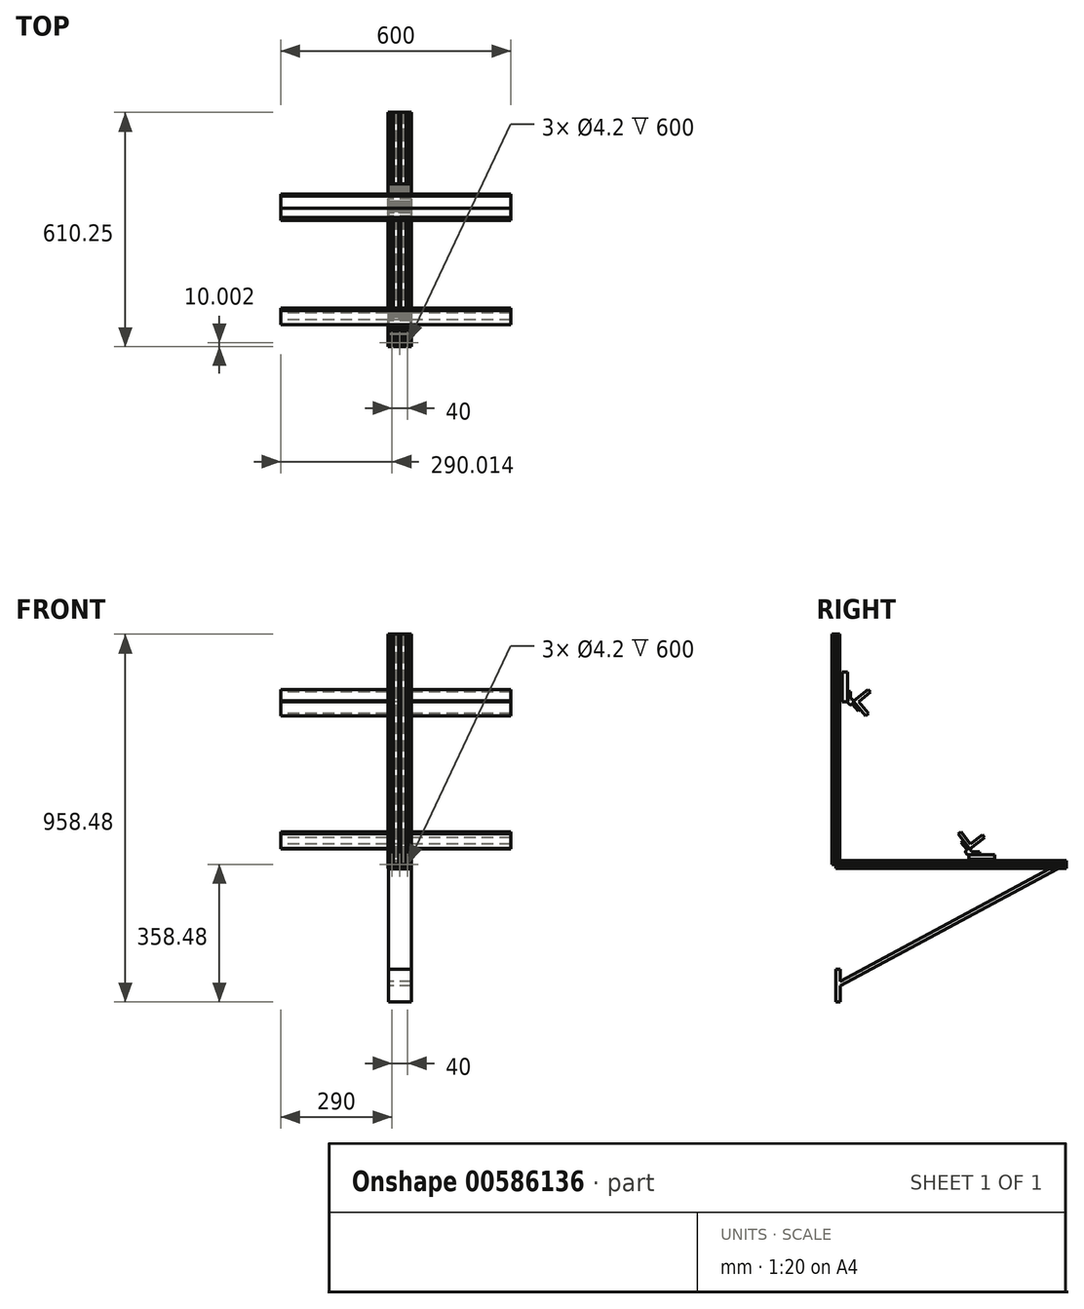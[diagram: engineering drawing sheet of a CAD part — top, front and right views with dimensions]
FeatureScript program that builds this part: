
annotation { "Feature Type Name" : "Feature", "Feature Type Description" : "" }
export const myFeature = defineFeature(function(context is Context, id is Id, definition is map)
    precondition{}
    {
        {
            var Q0;
            Q0=qCreatedBy(makeId("Front.planeOp"),FACE);
            var sketch = newSketch(context, id + "F0", { "sketchPlane" : qUnion([Q0])});
            skLineSegment(sketch, "E0.bottom", {"start": v(20, -10) * mm, "end": v(13, -10) * mm});
            skLineSegment(sketch, "E0.top", {"start": v(20, 10) * mm, "end": v(13, 10) * mm});
            skLineSegment(sketch, "E0.right", {"start": v(-20, -10) * mm, "end": v(-20, -3) * mm});
            skPoint(sketch, "E0.middle", {"position": v(0, 0) * mm});
            skLineSegment(sketch, "E1.bottom", {"start": v(-8, -3) * mm, "end": v(-12, -3) * mm});
            skLineSegment(sketch, "E1.top", {"start": v(-8, 3) * mm, "end": v(-12, 3) * mm});
            skLineSegment(sketch, "E1.left", {"start": v(-7, -2) * mm, "end": v(-7, 2) * mm});
            skLineSegment(sketch, "E1.right", {"start": v(-13, -2) * mm, "end": v(-13, 2) * mm});
            skPoint(sketch, "E1.middle", {"position": v(-10, 0) * mm});
            skLineSegment(sketch, "E2.bottom", {"start": v(8, -3) * mm, "end": v(12, -3) * mm});
            skLineSegment(sketch, "E2.top", {"start": v(8, 3) * mm, "end": v(12, 3) * mm});
            skLineSegment(sketch, "E2.left", {"start": v(7, -2) * mm, "end": v(7, 2) * mm});
            skLineSegment(sketch, "E2.right", {"start": v(13, -2) * mm, "end": v(13, 2) * mm});
            skPoint(sketch, "E2.middle", {"position": v(10, 0) * mm});
            skLineSegment(sketch, "E3.bottom", {"start": v(-3, -8) * mm, "end": v(-7, -8) * mm});
            skLineSegment(sketch, "E3.top", {"start": v(-3, 8) * mm, "end": v(-7, 8) * mm});
            skLineSegment(sketch, "E3.right", {"start": v(-18, -6) * mm, "end": v(-18, -3) * mm});
            skLineSegment(sketch, "E4.bottom", {"start": v(3, -8) * mm, "end": v(7, -8) * mm});
            skLineSegment(sketch, "E4.top", {"start": v(3, 8) * mm, "end": v(4, 8) * mm});
            skLineSegment(sketch, "E5.bottom", {"start": v(-20, 10) * mm, "end": v(-16, 10) * mm});
            skLineSegment(sketch, "E5.top", {"start": v(-18, 6) * mm, "end": v(-17, 6) * mm});
            skLineSegment(sketch, "E5.right", {"start": v(-16, 8) * mm, "end": v(-16, 7) * mm});
            skPoint(sketch, "E5.middle", {"position": v(-18, 8) * mm});
            skLineSegment(sketch, "E6.bottom", {"start": v(-20, 10) * mm, "end": v(-19, 10) * mm});
            skLineSegment(sketch, "E7.top", {"start": v(-1, -10) * mm, "end": v(0, -10) * mm});
            skLineSegment(sketch, "E8", {"start": v(-16, 7) * mm, "end": v(-12, 3) * mm});
            skLineSegment(sketch, "E9", {"start": v(-3, -8) * mm, "end": v(-8, -3) * mm});
            skLineSegment(sketch, "E10.MirrorCS", {"start": v(-16, -7) * mm, "end": v(-12, -3) * mm});
            skLineSegment(sketch, "E11.MirrorCS", {"start": v(-3, 8) * mm, "end": v(-8, 3) * mm});
            skLineSegment(sketch, "E12.MirrorCS", {"start": v(3, 8) * mm, "end": v(8, 3) * mm});
            skLineSegment(sketch, "E13.MirrorCS", {"start": v(3, -8) * mm, "end": v(8, -3) * mm});
            skLineSegment(sketch, "E14.bottom", {"start": v(20, 10) * mm, "end": v(16, 10) * mm});
            skPoint(sketch, "E14.middle", {"position": v(18, 8) * mm});
            skLineSegment(sketch, "E15.bottom", {"start": v(20, -10) * mm, "end": v(16, -10) * mm});
            skPoint(sketch, "E15.middle", {"position": v(18, -8) * mm});
            skPoint(sketch, "E16.orphan", {"position": v(13, 3) * mm});
            skLineSegment(sketch, "E17.trimOffspring", {"start": v(7, 2) * mm, "end": v(2, 7) * mm});
            skLineSegment(sketch, "E18.trimOffspring", {"start": v(7, -2) * mm, "end": v(2, -7) * mm});
            skPoint(sketch, "E19.orphan", {"position": v(13, -3) * mm});
            skPoint(sketch, "E20.orphan", {"position": v(7, 3) * mm});
            skPoint(sketch, "E21.orphan", {"position": v(7, -3) * mm});
            skPoint(sketch, "E22.orphan", {"position": v(19, -10) * mm});
            skPoint(sketch, "E7.left.start.orphan", {"position": v(-1, -9) * mm});
            skPoint(sketch, "E23.orphan", {"position": v(-2, -8) * mm});
            skPoint(sketch, "E24.orphan", {"position": v(-18, -8) * mm});
            skPoint(sketch, "E25.orphan", {"position": v(-19, -10) * mm});
            skPoint(sketch, "E26.orphan", {"position": v(-20, -9) * mm});
            skPoint(sketch, "E27.orphan", {"position": v(-16, 6) * mm});
            skPoint(sketch, "E28.orphan", {"position": v(-1, 10) * mm});
            skPoint(sketch, "E29.orphan", {"position": v(0, 9) * mm});
            skPoint(sketch, "E30.orphan", {"position": v(1, 10) * mm});
            skPoint(sketch, "E31.orphan", {"position": v(2, 8) * mm});
            skPoint(sketch, "E32.orphan", {"position": v(-2, 8) * mm});
            skPoint(sketch, "E33.orphan", {"position": v(0, -9) * mm});
            skPoint(sketch, "E34.orphan", {"position": v(1, -10) * mm});
            skPoint(sketch, "E35.orphan", {"position": v(2, -8) * mm});
            skLineSegment(sketch, "E36", {"start": v(-1, -8) * mm, "end": v(1, -8) * mm});
            skLineSegment(sketch, "E37", {"start": v(1, 8) * mm, "end": v(-1, 8) * mm});
            skLineSegment(sketch, "E38", {"start": v(-2, 7) * mm, "end": v(-1, 8) * mm});
            skLineSegment(sketch, "E39", {"start": v(2, 7) * mm, "end": v(1, 8) * mm});
            skLineSegment(sketch, "E40", {"start": v(-2, -7) * mm, "end": v(-1, -8) * mm});
            skLineSegment(sketch, "E41", {"start": v(2, -7) * mm, "end": v(1, -8) * mm});
            skPoint(sketch, "E42.orphan", {"position": v(-13, 3) * mm});
            skPoint(sketch, "E43.orphan", {"position": v(-7, 3) * mm});
            skPoint(sketch, "E44.orphan", {"position": v(-7, -3) * mm});
            skPoint(sketch, "E45.orphan", {"position": v(-13, -3) * mm});
            skLineSegment(sketch, "E46.trimOffspring", {"start": v(-13, 2) * mm, "end": v(-17, 6) * mm});
            skLineSegment(sketch, "E47.trimOffspring", {"start": v(-7, -2) * mm, "end": v(-2, -7) * mm});
            skLineSegment(sketch, "E48.trimOffspring", {"start": v(-7, 2) * mm, "end": v(-2, 7) * mm});
            skLineSegment(sketch, "E49.trimOffspring", {"start": v(-13, -2) * mm, "end": v(-17, -6) * mm});
            skLineSegment(sketch, "E50.bottom", {"start": v(-20, -10) * mm, "end": v(-16, -10) * mm});
            skLineSegment(sketch, "E50.top", {"start": v(-18, -6) * mm, "end": v(-17, -6) * mm});
            skLineSegment(sketch, "E50.left", {"start": v(-20, -10) * mm, "end": v(-20, -6) * mm});
            skLineSegment(sketch, "E50.right", {"start": v(-16, -8) * mm, "end": v(-16, -7) * mm});
            skPoint(sketch, "E51.orphan", {"position": v(-16, -6) * mm});
            skLineSegment(sketch, "E52", {"start": v(-13, -8) * mm, "end": v(-13, -10) * mm});
            skLineSegment(sketch, "E53", {"start": v(-7, -8) * mm, "end": v(-7, -10) * mm});
            skLineSegment(sketch, "E54", {"start": v(-18, 3) * mm, "end": v(-20, 3) * mm});
            skLineSegment(sketch, "E55", {"start": v(-18, -3) * mm, "end": v(-20, -3) * mm});
            skLineSegment(sketch, "E56", {"start": v(-13, 8) * mm, "end": v(-13, 10) * mm});
            skLineSegment(sketch, "E57", {"start": v(-7, 8) * mm, "end": v(-7, 10) * mm});
            skLineSegment(sketch, "E58.MirrorCS", {"start": v(13, -8) * mm, "end": v(13, -10) * mm});
            skLineSegment(sketch, "E59.MirrorCS", {"start": v(7, -8) * mm, "end": v(7, -10) * mm});
            skLineSegment(sketch, "E60.trimOffspring", {"start": v(-18, 3) * mm, "end": v(-18, 6) * mm});
            skLineSegment(sketch, "E61.trimOffspring", {"start": v(-20, 3) * mm, "end": v(-20, 7.62) * mm});
            skLineSegment(sketch, "E62.trimOffspring", {"start": v(-13, 10) * mm, "end": v(-20, 10) * mm});
            skLineSegment(sketch, "E63.trimOffspring", {"start": v(-13, 8) * mm, "end": v(-16, 8) * mm});
            skLineSegment(sketch, "E64.trimOffspring", {"start": v(-13, -8) * mm, "end": v(-16, -8) * mm});
            skLineSegment(sketch, "E65.trimOffspring", {"start": v(-13, -10) * mm, "end": v(-20, -10) * mm});
            skLineSegment(sketch, "E66.trimOffspring", {"start": v(13, -8) * mm, "end": v(16, -8) * mm});
            skLineSegment(sketch, "E67.trimOffspring", {"start": v(7, -10) * mm, "end": v(-7, -10) * mm});
            skCircle(sketch, "E68", {"center": v(-10, 0) * mm, "radius": 2.1 * mm});
            skCircle(sketch, "E69.MirrorC", {"center": v(10, 0) * mm, "radius": 2.1 * mm});
            skLineSegment(sketch, "E70.trimOffspring", {"start": v(-20, 7.62) * mm, "end": v(-20, 6) * mm});
            skLineSegment(sketch, "E71", {"start": v(-20, 10) * mm, "end": v(-20, 7.62) * mm});
            skLineSegment(sketch, "E72.MirrorCS", {"start": v(17, 8) * mm, "end": v(12, 3) * mm});
            skLineSegment(sketch, "E73.MirrorCS", {"start": v(13, 2) * mm, "end": v(18, 7) * mm});
            skLineSegment(sketch, "E74.MirrorCS", {"start": v(17, 8) * mm, "end": v(13, 8) * mm});
            skLineSegment(sketch, "E75.MirrorCS", {"start": v(17, -8) * mm, "end": v(12, -3) * mm});
            skLineSegment(sketch, "E76.MirrorCS", {"start": v(13, -2) * mm, "end": v(18, -7) * mm});
            skLineSegment(sketch, "E77.MirrorCS", {"start": v(17, -8) * mm, "end": v(13, -8) * mm});
            skLineSegment(sketch, "E78.MirrorCS", {"start": v(13, -10) * mm, "end": v(27, -10) * mm});
            skLineSegment(sketch, "E79.MirrorCS", {"start": v(40, 10) * mm, "end": v(39, 10) * mm});
            skLineSegment(sketch, "E80.MirrorCS", {"start": v(38, 6) * mm, "end": v(37, 6) * mm});
            skLineSegment(sketch, "E81.MirrorCS", {"start": v(36, 8) * mm, "end": v(36, 7) * mm});
            skLineSegment(sketch, "E82.MirrorCS", {"start": v(40, 10) * mm, "end": v(40, 7.62) * mm});
            skLineSegment(sketch, "E83.MirrorCS", {"start": v(21, -8) * mm, "end": v(19, -8) * mm});
            skLineSegment(sketch, "E84.MirrorCS", {"start": v(38, 3) * mm, "end": v(40, 3) * mm});
            skLineSegment(sketch, "E85.MirrorCS", {"start": v(36, -8) * mm, "end": v(36, -7) * mm});
            skLineSegment(sketch, "E86.MirrorCS", {"start": v(22, -7) * mm, "end": v(21, -8) * mm});
            skLineSegment(sketch, "E87.MirrorCS", {"start": v(22, 7) * mm, "end": v(21, 8) * mm});
            skLineSegment(sketch, "E88.MirrorCS", {"start": v(19, 8) * mm, "end": v(21, 8) * mm});
            skLineSegment(sketch, "E89.MirrorCS", {"start": v(38, -3) * mm, "end": v(40, -3) * mm});
            skLineSegment(sketch, "E90.MirrorCS", {"start": v(33, 8) * mm, "end": v(33, 10) * mm});
            skLineSegment(sketch, "E91.MirrorCS", {"start": v(38, -6) * mm, "end": v(37, -6) * mm});
            skLineSegment(sketch, "E92.MirrorCS", {"start": v(27, -8) * mm, "end": v(27, -10) * mm});
            skLineSegment(sketch, "E93.MirrorCS", {"start": v(27, 8) * mm, "end": v(27, 10) * mm});
            skLineSegment(sketch, "E94.MirrorCS", {"start": v(18, -7) * mm, "end": v(19, -8) * mm});
            skLineSegment(sketch, "E95.MirrorCS", {"start": v(18, 7) * mm, "end": v(19, 8) * mm});
            skLineSegment(sketch, "E96.MirrorCS", {"start": v(33, -8) * mm, "end": v(33, -10) * mm});
            skLineSegment(sketch, "E97.MirrorCS", {"start": v(21, -10) * mm, "end": v(20, -10) * mm});
            skLineSegment(sketch, "E98.MirrorCS", {"start": v(40, 7.62) * mm, "end": v(40, 6) * mm});
            skLineSegment(sketch, "E99.MirrorCS", {"start": v(40, -10) * mm, "end": v(40, -6) * mm});
            skPoint(sketch, "E100.MirrorP", {"position": v(38, -8) * mm});
            skPoint(sketch, "E101.MirrorP", {"position": v(20, 9) * mm});
            skPoint(sketch, "E102.MirrorP", {"position": v(30, 0) * mm});
            skPoint(sketch, "E103.MirrorP", {"position": v(20, -9) * mm});
            skLineSegment(sketch, "E104.MirrorCS", {"start": v(33, -8) * mm, "end": v(36, -8) * mm});
            skLineSegment(sketch, "E105.MirrorCS", {"start": v(27, -2) * mm, "end": v(27, 2) * mm});
            skLineSegment(sketch, "E106.MirrorCS", {"start": v(28, -3) * mm, "end": v(32, -3) * mm});
            skLineSegment(sketch, "E107.MirrorCS", {"start": v(28, 3) * mm, "end": v(32, 3) * mm});
            skLineSegment(sketch, "E108.MirrorCS", {"start": v(40, -10) * mm, "end": v(40, -3) * mm});
            skLineSegment(sketch, "E109.MirrorCS", {"start": v(38, -6) * mm, "end": v(38, -3) * mm});
            skLineSegment(sketch, "E110.MirrorCS", {"start": v(27, -2) * mm, "end": v(22, -7) * mm});
            skLineSegment(sketch, "E111.MirrorCS", {"start": v(40, 3) * mm, "end": v(40, 7.62) * mm});
            skLineSegment(sketch, "E112.MirrorCS", {"start": v(23, -8) * mm, "end": v(28, -3) * mm});
            skPoint(sketch, "E113.MirrorP", {"position": v(22, 8) * mm});
            skPoint(sketch, "E114.MirrorP", {"position": v(40, -9) * mm});
            skPoint(sketch, "E115.MirrorP", {"position": v(38, 8) * mm});
            skCircle(sketch, "E116.MirrorC", {"center": v(30, 0) * mm, "radius": 2.1 * mm});
            skPoint(sketch, "E117.MirrorP", {"position": v(27, -3) * mm});
            skPoint(sketch, "E118.MirrorP", {"position": v(27, 3) * mm});
            skPoint(sketch, "E119.MirrorP", {"position": v(22, -8) * mm});
            skPoint(sketch, "E120.MirrorP", {"position": v(36, -6) * mm});
            skLineSegment(sketch, "E121.MirrorCS", {"start": v(23, 8) * mm, "end": v(27, 8) * mm});
            skLineSegment(sketch, "E122.MirrorCS", {"start": v(23, -8) * mm, "end": v(27, -8) * mm});
            skLineSegment(sketch, "E123.MirrorCS", {"start": v(33, -2) * mm, "end": v(33, 2) * mm});
            skLineSegment(sketch, "E124.MirrorCS", {"start": v(23, 8) * mm, "end": v(28, 3) * mm});
            skLineSegment(sketch, "E125.MirrorCS", {"start": v(38, 3) * mm, "end": v(38, 6) * mm});
            skPoint(sketch, "E126.MirrorP", {"position": v(39, -10) * mm});
            skPoint(sketch, "E127.MirrorP", {"position": v(21, -9) * mm});
            skPoint(sketch, "E128.MirrorP", {"position": v(33, 3) * mm});
            skPoint(sketch, "E129.MirrorP", {"position": v(19, 10) * mm});
            skLineSegment(sketch, "E130.MirrorCS", {"start": v(33, -2) * mm, "end": v(37, -6) * mm});
            skLineSegment(sketch, "E131.MirrorCS", {"start": v(33, 8) * mm, "end": v(36, 8) * mm});
            skLineSegment(sketch, "E132.MirrorCS", {"start": v(40, -10) * mm, "end": v(36, -10) * mm});
            skLineSegment(sketch, "E133.MirrorCS", {"start": v(40, 10) * mm, "end": v(36, 10) * mm});
            skPoint(sketch, "E134.MirrorP", {"position": v(36, 6) * mm});
            skLineSegment(sketch, "E135.MirrorCS", {"start": v(27, 2) * mm, "end": v(22, 7) * mm});
            skLineSegment(sketch, "E136.MirrorCS", {"start": v(36, -7) * mm, "end": v(32, -3) * mm});
            skLineSegment(sketch, "E137.MirrorCS", {"start": v(33, 10) * mm, "end": v(40, 10) * mm});
            skLineSegment(sketch, "E138.MirrorCS", {"start": v(33, -10) * mm, "end": v(40, -10) * mm});
            skPoint(sketch, "E139.MirrorP", {"position": v(21, 10) * mm});
            skLineSegment(sketch, "E140.MirrorCS", {"start": v(33, 2) * mm, "end": v(37, 6) * mm});
            skLineSegment(sketch, "E141.MirrorCS", {"start": v(36, 7) * mm, "end": v(32, 3) * mm});
            skPoint(sketch, "E142.MirrorP", {"position": v(20, 0) * mm});
            skPoint(sketch, "E143.MirrorP", {"position": v(33, -3) * mm});
            skLineSegment(sketch, "E144.MirrorCS", {"start": v(0, 10) * mm, "end": v(1, 10) * mm});
            skLineSegment(sketch, "E145.MirrorCS", {"start": v(13, 8) * mm, "end": v(13, 10) * mm});
            skLineSegment(sketch, "E146.MirrorCS", {"start": v(7, 8) * mm, "end": v(7, 10) * mm});
            skLineSegment(sketch, "E147.trimOffspring", {"start": v(7, 10) * mm, "end": v(-7, 10) * mm});
            skLineSegment(sketch, "E148.trimOffspring", {"start": v(13, 10) * mm, "end": v(27, 10) * mm});
            skLineSegment(sketch, "E149.trimOffspring", {"start": v(13, 8) * mm, "end": v(16, 8) * mm});
            skLineSegment(sketch, "E150.trimOffspring", {"start": v(7, 8) * mm, "end": v(4, 8) * mm});
            skPoint(sketch, "E151.start.orphan", {"position": v(10, 3) * mm});
            skPoint(sketch, "E152.start.orphan", {"position": v(13, 0) * mm});
            skSolve(sketch);
        }
        {
            var Q0;
            Q0=qSketchRegion(id+"F0",true);
            extrude(context, id + "F1", {"entities" : qUnion([Q0]), "oppositeDirection" : true, "depth" : 600 * mm, "offsetDistance" : 25.4 * mm});
        }
        {
            var Q0;
            Q0=qCreatedBy(makeId("Top.planeOp"),FACE);
            var sketch = newSketch(context, id + "F2", { "sketchPlane" : qUnion([Q0])});
            skLineSegment(sketch, "E153.bottom", {"start": v(20.01, -10.25) * mm, "end": v(13.01, -10.25) * mm});
            skLineSegment(sketch, "E153.top", {"start": v(20.01, 9.75) * mm, "end": v(13.01, 9.75) * mm});
            skLineSegment(sketch, "E153.right", {"start": v(-19.99, -10.25) * mm, "end": v(-19.99, -3.25) * mm});
            skPoint(sketch, "E153.middle", {"position": v(0.01, -0.25) * mm});
            skLineSegment(sketch, "E154.bottom", {"start": v(-7.99, -3.25) * mm, "end": v(-11.99, -3.25) * mm});
            skLineSegment(sketch, "E154.top", {"start": v(-7.99, 2.75) * mm, "end": v(-11.99, 2.75) * mm});
            skLineSegment(sketch, "E154.left", {"start": v(-6.99, -2.25) * mm, "end": v(-6.99, 1.75) * mm});
            skLineSegment(sketch, "E154.right", {"start": v(-12.99, -2.25) * mm, "end": v(-12.99, 1.75) * mm});
            skPoint(sketch, "E154.middle", {"position": v(-9.99, -0.25) * mm});
            skLineSegment(sketch, "E155.bottom", {"start": v(8.01, -3.25) * mm, "end": v(12.01, -3.25) * mm});
            skLineSegment(sketch, "E155.top", {"start": v(8.01, 2.75) * mm, "end": v(12.01, 2.75) * mm});
            skLineSegment(sketch, "E155.left", {"start": v(7.01, -2.25) * mm, "end": v(7.01, 1.75) * mm});
            skLineSegment(sketch, "E155.right", {"start": v(13.01, -2.25) * mm, "end": v(13.01, 1.75) * mm});
            skPoint(sketch, "E155.middle", {"position": v(10.01, -0.25) * mm});
            skLineSegment(sketch, "E156.bottom", {"start": v(-2.99, -8.25) * mm, "end": v(-6.99, -8.25) * mm});
            skLineSegment(sketch, "E156.top", {"start": v(-2.99, 7.75) * mm, "end": v(-6.99, 7.75) * mm});
            skLineSegment(sketch, "E156.right", {"start": v(-17.99, -6.25) * mm, "end": v(-17.99, -3.25) * mm});
            skLineSegment(sketch, "E157.bottom", {"start": v(3.01, -8.25) * mm, "end": v(7.01, -8.25) * mm});
            skLineSegment(sketch, "E157.top", {"start": v(3.01, 7.75) * mm, "end": v(4.01, 7.75) * mm});
            skLineSegment(sketch, "E158.bottom", {"start": v(-19.99, 9.75) * mm, "end": v(-15.99, 9.75) * mm});
            skLineSegment(sketch, "E158.top", {"start": v(-17.99, 5.75) * mm, "end": v(-16.99, 5.75) * mm});
            skLineSegment(sketch, "E158.right", {"start": v(-15.99, 7.75) * mm, "end": v(-15.99, 6.75) * mm});
            skPoint(sketch, "E158.middle", {"position": v(-17.99, 7.75) * mm});
            skLineSegment(sketch, "E159.bottom", {"start": v(-19.99, 9.75) * mm, "end": v(-18.99, 9.75) * mm});
            skLineSegment(sketch, "E160.top", {"start": v(-0.99, -10.25) * mm, "end": v(0.01, -10.25) * mm});
            skLineSegment(sketch, "E161", {"start": v(-15.99, 6.75) * mm, "end": v(-11.99, 2.75) * mm});
            skLineSegment(sketch, "E162", {"start": v(-2.99, -8.25) * mm, "end": v(-7.99, -3.25) * mm});
            skLineSegment(sketch, "E163.MirrorCS", {"start": v(-15.99, -7.25) * mm, "end": v(-11.99, -3.25) * mm});
            skLineSegment(sketch, "E164.MirrorCS", {"start": v(-2.99, 7.75) * mm, "end": v(-7.99, 2.75) * mm});
            skLineSegment(sketch, "E165.MirrorCS", {"start": v(3.01, 7.75) * mm, "end": v(8.01, 2.75) * mm});
            skLineSegment(sketch, "E166.MirrorCS", {"start": v(3.01, -8.25) * mm, "end": v(8.01, -3.25) * mm});
            skLineSegment(sketch, "E167.bottom", {"start": v(20.01, 9.75) * mm, "end": v(16.01, 9.75) * mm});
            skPoint(sketch, "E167.middle", {"position": v(18.01, 7.75) * mm});
            skLineSegment(sketch, "E168.bottom", {"start": v(20.01, -10.25) * mm, "end": v(16.01, -10.25) * mm});
            skPoint(sketch, "E168.middle", {"position": v(18.01, -8.25) * mm});
            skPoint(sketch, "E169.orphan", {"position": v(13.01, 2.75) * mm});
            skLineSegment(sketch, "E170.trimOffspring", {"start": v(7.01, 1.75) * mm, "end": v(2.01, 6.75) * mm});
            skLineSegment(sketch, "E171.trimOffspring", {"start": v(7.01, -2.25) * mm, "end": v(2.01, -7.25) * mm});
            skPoint(sketch, "E172.orphan", {"position": v(13.01, -3.25) * mm});
            skPoint(sketch, "E173.orphan", {"position": v(7.01, 2.75) * mm});
            skPoint(sketch, "E174.orphan", {"position": v(7.01, -3.25) * mm});
            skPoint(sketch, "E175.orphan", {"position": v(19.01, -10.25) * mm});
            skPoint(sketch, "E160.left.start.orphan", {"position": v(-0.99, -9.25) * mm});
            skPoint(sketch, "E176.orphan", {"position": v(-1.99, -8.25) * mm});
            skPoint(sketch, "E177.orphan", {"position": v(-17.99, -8.25) * mm});
            skPoint(sketch, "E178.orphan", {"position": v(-18.99, -10.25) * mm});
            skPoint(sketch, "E179.orphan", {"position": v(-19.99, -9.25) * mm});
            skPoint(sketch, "E180.orphan", {"position": v(-15.99, 5.75) * mm});
            skPoint(sketch, "E181.orphan", {"position": v(-0.99, 9.75) * mm});
            skPoint(sketch, "E182.orphan", {"position": v(0.01, 8.75) * mm});
            skPoint(sketch, "E183.orphan", {"position": v(1.01, 9.75) * mm});
            skPoint(sketch, "E184.orphan", {"position": v(2.01, 7.75) * mm});
            skPoint(sketch, "E185.orphan", {"position": v(-1.99, 7.75) * mm});
            skPoint(sketch, "E186.orphan", {"position": v(0.01, -9.25) * mm});
            skPoint(sketch, "E187.orphan", {"position": v(1.01, -10.25) * mm});
            skPoint(sketch, "E188.orphan", {"position": v(2.01, -8.25) * mm});
            skLineSegment(sketch, "E189", {"start": v(-0.99, -8.25) * mm, "end": v(1.01, -8.25) * mm});
            skLineSegment(sketch, "E190", {"start": v(1.01, 7.75) * mm, "end": v(-0.99, 7.75) * mm});
            skLineSegment(sketch, "E191", {"start": v(-1.99, 6.75) * mm, "end": v(-0.99, 7.75) * mm});
            skLineSegment(sketch, "E192", {"start": v(2.01, 6.75) * mm, "end": v(1.01, 7.75) * mm});
            skLineSegment(sketch, "E193", {"start": v(-1.99, -7.25) * mm, "end": v(-0.99, -8.25) * mm});
            skLineSegment(sketch, "E194", {"start": v(2.01, -7.25) * mm, "end": v(1.01, -8.25) * mm});
            skPoint(sketch, "E195.orphan", {"position": v(-12.99, 2.75) * mm});
            skPoint(sketch, "E196.orphan", {"position": v(-6.99, 2.75) * mm});
            skPoint(sketch, "E197.orphan", {"position": v(-6.99, -3.25) * mm});
            skPoint(sketch, "E198.orphan", {"position": v(-12.99, -3.25) * mm});
            skLineSegment(sketch, "E199.trimOffspring", {"start": v(-12.99, 1.75) * mm, "end": v(-16.99, 5.75) * mm});
            skLineSegment(sketch, "E200.trimOffspring", {"start": v(-6.99, -2.25) * mm, "end": v(-1.99, -7.25) * mm});
            skLineSegment(sketch, "E201.trimOffspring", {"start": v(-6.99, 1.75) * mm, "end": v(-1.99, 6.75) * mm});
            skLineSegment(sketch, "E202.trimOffspring", {"start": v(-12.99, -2.25) * mm, "end": v(-16.99, -6.25) * mm});
            skLineSegment(sketch, "E203.bottom", {"start": v(-19.99, -10.25) * mm, "end": v(-15.99, -10.25) * mm});
            skLineSegment(sketch, "E203.top", {"start": v(-17.99, -6.25) * mm, "end": v(-16.99, -6.25) * mm});
            skLineSegment(sketch, "E203.left", {"start": v(-19.99, -10.25) * mm, "end": v(-19.99, -6.25) * mm});
            skLineSegment(sketch, "E203.right", {"start": v(-15.99, -8.25) * mm, "end": v(-15.99, -7.25) * mm});
            skPoint(sketch, "E204.orphan", {"position": v(-15.99, -6.25) * mm});
            skLineSegment(sketch, "E205", {"start": v(-12.99, -8.25) * mm, "end": v(-12.99, -10.25) * mm});
            skLineSegment(sketch, "E206", {"start": v(-6.99, -8.25) * mm, "end": v(-6.99, -10.25) * mm});
            skLineSegment(sketch, "E207", {"start": v(-17.99, 2.75) * mm, "end": v(-19.99, 2.75) * mm});
            skLineSegment(sketch, "E208", {"start": v(-17.99, -3.25) * mm, "end": v(-19.99, -3.25) * mm});
            skLineSegment(sketch, "E209", {"start": v(-12.99, 7.75) * mm, "end": v(-12.99, 9.75) * mm});
            skLineSegment(sketch, "E210", {"start": v(-6.99, 7.75) * mm, "end": v(-6.99, 9.75) * mm});
            skLineSegment(sketch, "E211.MirrorCS", {"start": v(13.01, -8.25) * mm, "end": v(13.01, -10.25) * mm});
            skLineSegment(sketch, "E212.MirrorCS", {"start": v(7.01, -8.25) * mm, "end": v(7.01, -10.25) * mm});
            skLineSegment(sketch, "E213.trimOffspring", {"start": v(-17.99, 2.75) * mm, "end": v(-17.99, 5.75) * mm});
            skLineSegment(sketch, "E214.trimOffspring", {"start": v(-19.99, 2.75) * mm, "end": v(-19.99, 7.37) * mm});
            skLineSegment(sketch, "E215.trimOffspring", {"start": v(-12.99, 9.75) * mm, "end": v(-19.99, 9.75) * mm});
            skLineSegment(sketch, "E216.trimOffspring", {"start": v(-12.99, 7.75) * mm, "end": v(-15.99, 7.75) * mm});
            skLineSegment(sketch, "E217.trimOffspring", {"start": v(-12.99, -8.25) * mm, "end": v(-15.99, -8.25) * mm});
            skLineSegment(sketch, "E218.trimOffspring", {"start": v(-12.99, -10.25) * mm, "end": v(-19.99, -10.25) * mm});
            skLineSegment(sketch, "E219.trimOffspring", {"start": v(13.01, -8.25) * mm, "end": v(16.01, -8.25) * mm});
            skLineSegment(sketch, "E220.trimOffspring", {"start": v(7.01, -10.25) * mm, "end": v(-6.99, -10.25) * mm});
            skCircle(sketch, "E221", {"center": v(-9.99, -0.25) * mm, "radius": 2.1 * mm});
            skCircle(sketch, "E222.MirrorC", {"center": v(10.01, -0.25) * mm, "radius": 2.1 * mm});
            skLineSegment(sketch, "E223.trimOffspring", {"start": v(-19.99, 7.37) * mm, "end": v(-19.99, 5.75) * mm});
            skLineSegment(sketch, "E224", {"start": v(-19.99, 9.75) * mm, "end": v(-19.99, 7.37) * mm});
            skLineSegment(sketch, "E225.MirrorCS", {"start": v(17.01, 7.75) * mm, "end": v(12.01, 2.75) * mm});
            skLineSegment(sketch, "E226.MirrorCS", {"start": v(13.01, 1.75) * mm, "end": v(18.01, 6.75) * mm});
            skLineSegment(sketch, "E227.MirrorCS", {"start": v(17.01, 7.75) * mm, "end": v(13.01, 7.75) * mm});
            skLineSegment(sketch, "E228.MirrorCS", {"start": v(17.01, -8.25) * mm, "end": v(12.01, -3.25) * mm});
            skLineSegment(sketch, "E229.MirrorCS", {"start": v(13.01, -2.25) * mm, "end": v(18.01, -7.25) * mm});
            skLineSegment(sketch, "E230.MirrorCS", {"start": v(17.01, -8.25) * mm, "end": v(13.01, -8.25) * mm});
            skLineSegment(sketch, "E231.MirrorCS", {"start": v(13.01, -10.25) * mm, "end": v(27.01, -10.25) * mm});
            skLineSegment(sketch, "E232.MirrorCS", {"start": v(40.01, 9.75) * mm, "end": v(39.01, 9.75) * mm});
            skLineSegment(sketch, "E233.MirrorCS", {"start": v(38.01, 5.75) * mm, "end": v(37.01, 5.75) * mm});
            skLineSegment(sketch, "E234.MirrorCS", {"start": v(36.01, 7.75) * mm, "end": v(36.01, 6.75) * mm});
            skLineSegment(sketch, "E235.MirrorCS", {"start": v(40.01, 9.75) * mm, "end": v(40.01, 7.37) * mm});
            skLineSegment(sketch, "E236.MirrorCS", {"start": v(21.01, -8.25) * mm, "end": v(19.01, -8.25) * mm});
            skLineSegment(sketch, "E237.MirrorCS", {"start": v(38.01, 2.75) * mm, "end": v(40.01, 2.75) * mm});
            skLineSegment(sketch, "E238.MirrorCS", {"start": v(36.01, -8.25) * mm, "end": v(36.01, -7.25) * mm});
            skLineSegment(sketch, "E239.MirrorCS", {"start": v(22.01, -7.25) * mm, "end": v(21.01, -8.25) * mm});
            skLineSegment(sketch, "E240.MirrorCS", {"start": v(22.01, 6.75) * mm, "end": v(21.01, 7.75) * mm});
            skLineSegment(sketch, "E241.MirrorCS", {"start": v(19.01, 7.75) * mm, "end": v(21.01, 7.75) * mm});
            skLineSegment(sketch, "E242.MirrorCS", {"start": v(38.01, -3.25) * mm, "end": v(40.01, -3.25) * mm});
            skLineSegment(sketch, "E243.MirrorCS", {"start": v(33.01, 7.75) * mm, "end": v(33.01, 9.75) * mm});
            skLineSegment(sketch, "E244.MirrorCS", {"start": v(38.01, -6.25) * mm, "end": v(37.01, -6.25) * mm});
            skLineSegment(sketch, "E245.MirrorCS", {"start": v(27.01, -8.25) * mm, "end": v(27.01, -10.25) * mm});
            skLineSegment(sketch, "E246.MirrorCS", {"start": v(27.01, 7.75) * mm, "end": v(27.01, 9.75) * mm});
            skLineSegment(sketch, "E247.MirrorCS", {"start": v(18.01, -7.25) * mm, "end": v(19.01, -8.25) * mm});
            skLineSegment(sketch, "E248.MirrorCS", {"start": v(18.01, 6.75) * mm, "end": v(19.01, 7.75) * mm});
            skLineSegment(sketch, "E249.MirrorCS", {"start": v(33.01, -8.25) * mm, "end": v(33.01, -10.25) * mm});
            skLineSegment(sketch, "E250.MirrorCS", {"start": v(21.01, -10.25) * mm, "end": v(20.01, -10.25) * mm});
            skLineSegment(sketch, "E251.MirrorCS", {"start": v(40.01, 7.37) * mm, "end": v(40.01, 5.75) * mm});
            skLineSegment(sketch, "E252.MirrorCS", {"start": v(40.01, -10.25) * mm, "end": v(40.01, -6.25) * mm});
            skPoint(sketch, "E253.MirrorP", {"position": v(38.01, -8.25) * mm});
            skPoint(sketch, "E254.MirrorP", {"position": v(20.01, 8.75) * mm});
            skPoint(sketch, "E255.MirrorP", {"position": v(30.01, -0.25) * mm});
            skPoint(sketch, "E256.MirrorP", {"position": v(20.01, -9.25) * mm});
            skLineSegment(sketch, "E257.MirrorCS", {"start": v(33.01, -8.25) * mm, "end": v(36.01, -8.25) * mm});
            skLineSegment(sketch, "E258.MirrorCS", {"start": v(27.01, -2.25) * mm, "end": v(27.01, 1.75) * mm});
            skLineSegment(sketch, "E259.MirrorCS", {"start": v(28.01, -3.25) * mm, "end": v(32.01, -3.25) * mm});
            skLineSegment(sketch, "E260.MirrorCS", {"start": v(28.01, 2.75) * mm, "end": v(32.01, 2.75) * mm});
            skLineSegment(sketch, "E261.MirrorCS", {"start": v(40.01, -10.25) * mm, "end": v(40.01, -3.25) * mm});
            skLineSegment(sketch, "E262.MirrorCS", {"start": v(38.01, -6.25) * mm, "end": v(38.01, -3.25) * mm});
            skLineSegment(sketch, "E263.MirrorCS", {"start": v(27.01, -2.25) * mm, "end": v(22.01, -7.25) * mm});
            skLineSegment(sketch, "E264.MirrorCS", {"start": v(40.01, 2.75) * mm, "end": v(40.01, 7.37) * mm});
            skLineSegment(sketch, "E265.MirrorCS", {"start": v(23.01, -8.25) * mm, "end": v(28.01, -3.25) * mm});
            skPoint(sketch, "E266.MirrorP", {"position": v(22.01, 7.75) * mm});
            skPoint(sketch, "E267.MirrorP", {"position": v(40.01, -9.25) * mm});
            skPoint(sketch, "E268.MirrorP", {"position": v(38.01, 7.75) * mm});
            skCircle(sketch, "E269.MirrorC", {"center": v(30.01, -0.25) * mm, "radius": 2.1 * mm});
            skPoint(sketch, "E270.MirrorP", {"position": v(27.01, -3.25) * mm});
            skPoint(sketch, "E271.MirrorP", {"position": v(27.01, 2.75) * mm});
            skPoint(sketch, "E272.MirrorP", {"position": v(22.01, -8.25) * mm});
            skPoint(sketch, "E273.MirrorP", {"position": v(36.01, -6.25) * mm});
            skLineSegment(sketch, "E274.MirrorCS", {"start": v(23.01, 7.75) * mm, "end": v(27.01, 7.75) * mm});
            skLineSegment(sketch, "E275.MirrorCS", {"start": v(23.01, -8.25) * mm, "end": v(27.01, -8.25) * mm});
            skLineSegment(sketch, "E276.MirrorCS", {"start": v(33.01, -2.25) * mm, "end": v(33.01, 1.75) * mm});
            skLineSegment(sketch, "E277.MirrorCS", {"start": v(23.01, 7.75) * mm, "end": v(28.01, 2.75) * mm});
            skLineSegment(sketch, "E278.MirrorCS", {"start": v(38.01, 2.75) * mm, "end": v(38.01, 5.75) * mm});
            skPoint(sketch, "E279.MirrorP", {"position": v(39.01, -10.25) * mm});
            skPoint(sketch, "E280.MirrorP", {"position": v(21.01, -9.25) * mm});
            skPoint(sketch, "E281.MirrorP", {"position": v(33.01, 2.75) * mm});
            skPoint(sketch, "E282.MirrorP", {"position": v(19.01, 9.75) * mm});
            skLineSegment(sketch, "E283.MirrorCS", {"start": v(33.01, -2.25) * mm, "end": v(37.01, -6.25) * mm});
            skLineSegment(sketch, "E284.MirrorCS", {"start": v(33.01, 7.75) * mm, "end": v(36.01, 7.75) * mm});
            skLineSegment(sketch, "E285.MirrorCS", {"start": v(40.01, -10.25) * mm, "end": v(36.01, -10.25) * mm});
            skLineSegment(sketch, "E286.MirrorCS", {"start": v(40.01, 9.75) * mm, "end": v(36.01, 9.75) * mm});
            skPoint(sketch, "E287.MirrorP", {"position": v(36.01, 5.75) * mm});
            skLineSegment(sketch, "E288.MirrorCS", {"start": v(27.01, 1.75) * mm, "end": v(22.01, 6.75) * mm});
            skLineSegment(sketch, "E289.MirrorCS", {"start": v(36.01, -7.25) * mm, "end": v(32.01, -3.25) * mm});
            skLineSegment(sketch, "E290.MirrorCS", {"start": v(33.01, 9.75) * mm, "end": v(40.01, 9.75) * mm});
            skLineSegment(sketch, "E291.MirrorCS", {"start": v(33.01, -10.25) * mm, "end": v(40.01, -10.25) * mm});
            skPoint(sketch, "E292.MirrorP", {"position": v(21.01, 9.75) * mm});
            skLineSegment(sketch, "E293.MirrorCS", {"start": v(33.01, 1.75) * mm, "end": v(37.01, 5.75) * mm});
            skLineSegment(sketch, "E294.MirrorCS", {"start": v(36.01, 6.75) * mm, "end": v(32.01, 2.75) * mm});
            skPoint(sketch, "E295.MirrorP", {"position": v(20.01, -0.25) * mm});
            skPoint(sketch, "E296.MirrorP", {"position": v(33.01, -3.25) * mm});
            skLineSegment(sketch, "E297.MirrorCS", {"start": v(0.01, 9.75) * mm, "end": v(1.01, 9.75) * mm});
            skLineSegment(sketch, "E298.MirrorCS", {"start": v(13.01, 7.75) * mm, "end": v(13.01, 9.75) * mm});
            skLineSegment(sketch, "E299.MirrorCS", {"start": v(7.01, 7.75) * mm, "end": v(7.01, 9.75) * mm});
            skLineSegment(sketch, "E300.trimOffspring", {"start": v(7.01, 9.75) * mm, "end": v(-6.99, 9.75) * mm});
            skLineSegment(sketch, "E301.trimOffspring", {"start": v(13.01, 9.75) * mm, "end": v(27.01, 9.75) * mm});
            skLineSegment(sketch, "E302.trimOffspring", {"start": v(13.01, 7.75) * mm, "end": v(16.01, 7.75) * mm});
            skLineSegment(sketch, "E303.trimOffspring", {"start": v(7.01, 7.75) * mm, "end": v(4.01, 7.75) * mm});
            skPoint(sketch, "E304.start.orphan", {"position": v(10.01, 2.75) * mm});
            skPoint(sketch, "E305.start.orphan", {"position": v(13.01, -0.25) * mm});
            skSolve(sketch);
        }
        {
            var Q0;
            Q0=qSketchRegion(id+"F2",true);
            extrude(context, id + "F3", {"entities" : qUnion([Q0]), "operationType" : NewBodyOperationType.ADD, "depth" : 600 * mm, "offsetDistance" : 25.4 * mm});
        }
        {
            var Q0;
            Q0=qCreatedBy(makeId("Right.planeOp"),FACE);
            var sketch = newSketch(context, id + "F4", { "sketchPlane" : qUnion([Q0])});
            skLineSegment(sketch, "E306.right", {"start": v(577.1, -11.57) * mm, "end": v(577.1, -11.74) * mm});
            skLineSegment(sketch, "E307", {"start": v(555.61, -11.57) * mm, "end": v(11.28, -304.62) * mm});
            skLineSegment(sketch, "E308", {"start": v(577.42, -11.57) * mm, "end": v(11.28, -316.37) * mm});
            skLineSegment(sketch, "E309", {"start": v(0, -322.44) * mm, "end": v(0, -310.7) * mm});
            skLineSegment(sketch, "E310", {"start": v(555.61, -11.57) * mm, "end": v(577.42, -11.57) * mm});
            skPoint(sketch, "E311.orphan", {"position": v(577.1, 0) * mm});
            skPoint(sketch, "E312.orphan", {"position": v(598.9, 0) * mm});
            skLineSegment(sketch, "E313.top", {"start": v(0, -358.48) * mm, "end": v(11.28, -358.48) * mm});
            skLineSegment(sketch, "E313.left", {"start": v(0, -291.08) * mm, "end": v(0, -358.48) * mm});
            skLineSegment(sketch, "E313.right", {"start": v(11.28, -291.08) * mm, "end": v(11.28, -304.62) * mm});
            skLineSegment(sketch, "E314.top", {"start": v(11.28, -272.73) * mm, "end": v(0, -272.73) * mm});
            skLineSegment(sketch, "E314.left", {"start": v(11.28, -291.08) * mm, "end": v(11.28, -272.73) * mm});
            skLineSegment(sketch, "E314.right", {"start": v(0, -291.08) * mm, "end": v(0, -272.73) * mm});
            skLineSegment(sketch, "E315.trimOffspring", {"start": v(11.28, -316.37) * mm, "end": v(11.28, -358.48) * mm});
            skSolve(sketch);
        }
        {
            var Q0;
            Q0=qSketchRegion(id+"F4",true);
            extrude(context, id + "F5", {"entities" : qUnion([Q0]), "depth" : 40.4 * mm, "offsetDistance" : 25.4 * mm, "hasSecondDirection" : true, "secondDirectionOppositeDirection" : true, "secondDirectionDepth" : 19.8 * mm});
        }
        {
            var Q0;
            Q0=qCreatedBy(makeId("Right.planeOp"),FACE);
            var sketch = newSketch(context, id + "F6", { "sketchPlane" : qUnion([Q0])});
            skLineSegment(sketch, "E316", {"start": v(31.2, 420.16) * mm, "end": v(339.93, 26.86) * mm});
            skLineSegment(sketch, "E317.bottom", {"start": v(345.64, 13.63) * mm, "end": v(413.27, 13.63) * mm});
            skLineSegment(sketch, "E317.top", {"start": v(345.64, 25.03) * mm, "end": v(413.27, 25.03) * mm});
            skLineSegment(sketch, "E317.left", {"start": v(345.64, 13.63) * mm, "end": v(345.64, 25.03) * mm});
            skLineSegment(sketch, "E317.right", {"start": v(413.27, 13.63) * mm, "end": v(413.27, 25.03) * mm});
            skCircle(sketch, "E318", {"center": v(345.64, 32.7) * mm, "radius": 7.67 * mm});
            skLineSegment(sketch, "E319", {"start": v(345.64, 32.7) * mm, "end": v(326.32, 57.32) * mm});
            skLineSegment(sketch, "E320", {"start": v(326.32, 57.32) * mm, "end": v(330.53, 60.62) * mm});
            skLineSegment(sketch, "E321", {"start": v(330.53, 60.62) * mm, "end": v(346.46, 40.32) * mm});
            skLineSegment(sketch, "E322", {"start": v(185.56, 223.5) * mm, "end": v(222.86, 252.78) * mm});
            skLineSegment(sketch, "E323.MirrorCS", {"start": v(38.23, 424.32) * mm, "end": v(57.55, 399.7) * mm});
            skLineSegment(sketch, "E324.MirrorCS", {"start": v(57.55, 399.7) * mm, "end": v(61.76, 403.01) * mm});
            skLineSegment(sketch, "E325.MirrorCS", {"start": v(61.76, 403.01) * mm, "end": v(45.83, 423.3) * mm});
            skCircle(sketch, "E326.MirrorC", {"center": v(38.23, 424.32) * mm, "radius": 7.67 * mm});
            skLineSegment(sketch, "E327.bottom", {"start": v(30.56, 424.32) * mm, "end": v(15.48, 424.32) * mm});
            skLineSegment(sketch, "E327.top", {"start": v(30.56, 502) * mm, "end": v(15.48, 502) * mm});
            skLineSegment(sketch, "E327.left", {"start": v(30.56, 424.32) * mm, "end": v(30.56, 502) * mm});
            skLineSegment(sketch, "E327.right", {"start": v(15.48, 424.32) * mm, "end": v(15.48, 502) * mm});
            skLineSegment(sketch, "E328.bottom", {"start": v(38.23, 424.32) * mm, "end": v(38.23, 424.32) * mm});
            skLineSegment(sketch, "E328.top", {"start": v(38.23, 451.2) * mm, "end": v(38.23, 451.2) * mm});
            skLineSegment(sketch, "E328.left", {"start": v(38.23, 424.32) * mm, "end": v(38.23, 451.2) * mm});
            skLineSegment(sketch, "E328.right", {"start": v(38.23, 424.32) * mm, "end": v(38.23, 451.2) * mm});
            skLineSegment(sketch, "E329.right", {"start": v(30.56, 451.2) * mm, "end": v(30.56, 451.2) * mm});
            skLineSegment(sketch, "E330", {"start": v(345.64, 32.7) * mm, "end": v(374.18, 32.7) * mm});
            skLineSegment(sketch, "E331.bottom", {"start": v(38.23, 451.2) * mm, "end": v(30.95, 451.2) * mm});
            skLineSegment(sketch, "E331.top", {"start": v(38.23, 426.74) * mm, "end": v(30.95, 426.74) * mm});
            skLineSegment(sketch, "E331.left", {"start": v(38.23, 451.2) * mm, "end": v(38.23, 426.74) * mm});
            skLineSegment(sketch, "E331.right", {"start": v(30.95, 451.2) * mm, "end": v(30.95, 426.74) * mm});
            skLineSegment(sketch, "E332.bottom", {"start": v(374.18, 32.7) * mm, "end": v(347.68, 32.7) * mm});
            skLineSegment(sketch, "E332.top", {"start": v(374.18, 25.3) * mm, "end": v(347.68, 25.3) * mm});
            skLineSegment(sketch, "E332.left", {"start": v(374.18, 32.7) * mm, "end": v(374.18, 25.3) * mm});
            skLineSegment(sketch, "E332.right", {"start": v(347.68, 32.7) * mm, "end": v(347.68, 25.3) * mm});
            skSolve(sketch);
        }
        {
            var Q0;
            Q0=qSketchRegion(id+"F6",true);
            extrude(context, id + "F7", {"entities" : qUnion([Q0]), "depth" : 40.64 * mm, "offsetDistance" : 25.4 * mm, "hasSecondDirection" : true, "secondDirectionOppositeDirection" : true, "secondDirectionDepth" : 20.57 * mm});
        }
        {
            var Q0;
            Q0=qCreatedBy(makeId("Right.planeOp"),FACE);
            var sketch = newSketch(context, id + "F8", { "sketchPlane" : qUnion([Q0])});
            skLineSegment(sketch, "E333", {"start": v(46.93, 424.2) * mm, "end": v(77.13, 387.33) * mm});
            skLineSegment(sketch, "E334", {"start": v(77.13, 387.33) * mm, "end": v(84.4, 393.3) * mm});
            skLineSegment(sketch, "E335", {"start": v(84.4, 393.3) * mm, "end": v(59.18, 424.09) * mm});
            skLineSegment(sketch, "E336", {"start": v(59.18, 424.09) * mm, "end": v(89.67, 449.06) * mm});
            skLineSegment(sketch, "E337", {"start": v(89.67, 449.06) * mm, "end": v(83.8, 456.22) * mm});
            skLineSegment(sketch, "E338", {"start": v(83.8, 456.22) * mm, "end": v(46.93, 426.01) * mm});
            skLineSegment(sketch, "E339", {"start": v(46.93, 426.01) * mm, "end": v(46.93, 424.2) * mm});
            skLineSegment(sketch, "E340.MirrorCS", {"start": v(349.35, 40.75) * mm, "end": v(347.59, 41.18) * mm});
            skLineSegment(sketch, "E341.MirrorCS", {"start": v(387.45, 69.4) * mm, "end": v(349.35, 40.75) * mm});
            skLineSegment(sketch, "E342.MirrorCS", {"start": v(350.4, 53.1) * mm, "end": v(381.9, 76.8) * mm});
            skLineSegment(sketch, "E343.MirrorCS", {"start": v(326.47, 84.93) * mm, "end": v(350.4, 53.1) * mm});
            skLineSegment(sketch, "E344.MirrorCS", {"start": v(347.59, 41.18) * mm, "end": v(318.95, 79.27) * mm});
            skLineSegment(sketch, "E345.MirrorCS", {"start": v(381.9, 76.8) * mm, "end": v(387.45, 69.4) * mm});
            skLineSegment(sketch, "E346.MirrorCS", {"start": v(318.95, 79.27) * mm, "end": v(326.47, 84.93) * mm});
            skSolve(sketch);
        }
        {
            var Q0;
            Q0=qSketchRegion(id+"F8",true);
            extrude(context, id + "F9", {"entities" : qUnion([Q0]), "depth" : 300 * mm, "offsetDistance" : 25.4 * mm, "hasSecondDirection" : true, "secondDirectionOppositeDirection" : true, "secondDirectionDepth" : 300 * mm});
        }
    });
